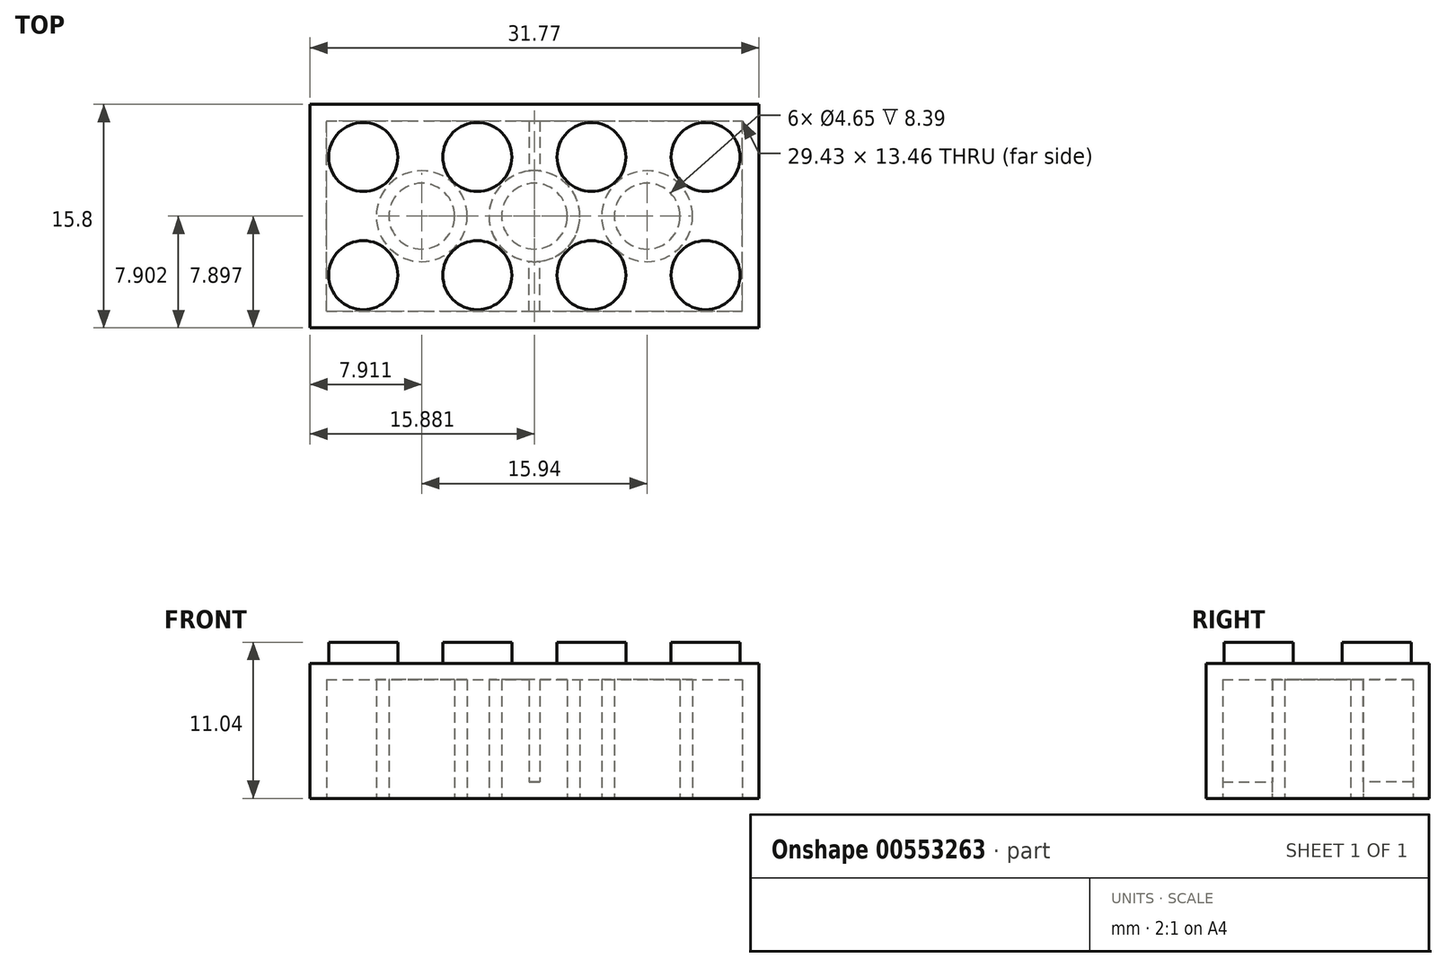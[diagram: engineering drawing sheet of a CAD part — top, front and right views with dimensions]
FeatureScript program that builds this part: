
annotation { "Feature Type Name" : "Feature", "Feature Type Description" : "" }
export const myFeature = defineFeature(function(context is Context, id is Id, definition is map)
    precondition{}
    {
        {
            var Q0;
            Q0=qCreatedBy(makeId("Top.planeOp"),FACE);
            var sketch = newSketch(context, id + "F0", { "sketchPlane" : qUnion([Q0])});
            skLineSegment(sketch, "E0.bottom", {"start": v(-13.15, 22.82) * mm, "end": v(18.62, 22.82) * mm});
            skLineSegment(sketch, "E0.top", {"start": v(-13.15, 7.02) * mm, "end": v(18.62, 7.02) * mm});
            skLineSegment(sketch, "E0.left", {"start": v(-13.15, 22.82) * mm, "end": v(-13.15, 7.02) * mm});
            skLineSegment(sketch, "E0.right", {"start": v(18.62, 22.82) * mm, "end": v(18.62, 7.02) * mm});
            skLineSegment(sketch, "E1.bottom", {"start": v(-11.98, 8.2) * mm, "end": v(17.45, 8.2) * mm});
            skLineSegment(sketch, "E1.top", {"start": v(-11.98, 21.65) * mm, "end": v(17.45, 21.65) * mm});
            skLineSegment(sketch, "E1.left", {"start": v(-11.98, 8.2) * mm, "end": v(-11.98, 21.65) * mm});
            skLineSegment(sketch, "E1.right", {"start": v(17.45, 8.2) * mm, "end": v(17.45, 21.65) * mm});
            skCircle(sketch, "E2", {"center": v(2.73, 14.92) * mm, "radius": 3.21 * mm});
            skCircle(sketch, "E3", {"center": v(10.7, 14.92) * mm, "radius": 3.21 * mm});
            skCircle(sketch, "E4", {"center": v(-5.24, 14.92) * mm, "radius": 3.21 * mm});
            skCircle(sketch, "E5", {"center": v(-5.24, 14.92) * mm, "radius": 2.32 * mm});
            skCircle(sketch, "E6", {"center": v(2.73, 14.92) * mm, "radius": 2.32 * mm});
            skCircle(sketch, "E7", {"center": v(10.7, 14.92) * mm, "radius": 2.32 * mm});
            skLineSegment(sketch, "E8", {"start": v(2.36, 8.2) * mm, "end": v(2.36, 11.72) * mm});
            skLineSegment(sketch, "E9", {"start": v(3.1, 8.2) * mm, "end": v(3.1, 11.72) * mm});
            skLineSegment(sketch, "E10", {"start": v(2.36, 21.65) * mm, "end": v(2.36, 18.11) * mm});
            skLineSegment(sketch, "E11", {"start": v(3.1, 21.65) * mm, "end": v(3.1, 18.11) * mm});
            skSolve(sketch);
        }
        {
            var Q0;
            Q0=qSketchRegion(id+"F0",true);
            var Q1;
            {var subQ3=sQuery(id+"F0.wireOp",EDGE,"E1.left");Q1=makeQuery(id+"F0.imprint","IMPRINT",FACE,{"disambiguationData":[TD([[makeQuery(id+"F0.imprint","IMPRINT",EDGE,{"derivedFrom":subQ3}),-1.0]])]});}
            var Q2;
            {var subQ3=sQuery(id+"F0.wireOp",EDGE,"E1.right");Q2=makeQuery(id+"F0.imprint","IMPRINT",FACE,{"disambiguationData":[TD([[makeQuery(id+"F0.imprint","IMPRINT",EDGE,{"derivedFrom":subQ3}),1.0]])]});}
            var Q3;
            Q3=makeQuery(id+"F0.imprint","IMPRINT",FACE,{"disambiguationData":[TD([[makeQuery(id+"F0.imprint","IMPRINT",EDGE,{"derivedFrom":sQuery(id+"F0.wireOp",EDGE,"E7")}),1.0]])]});
            var Q4;
            Q4=makeQuery(id+"F0.imprint","IMPRINT",FACE,{"disambiguationData":[TD([[makeQuery(id+"F0.imprint","IMPRINT",EDGE,{"derivedFrom":sQuery(id+"F0.wireOp",EDGE,"E5")}),1.0]])]});
            var Q5;
            Q5=makeQuery(id+"F0.imprint","IMPRINT",FACE,{"disambiguationData":[TD([[makeQuery(id+"F0.imprint","IMPRINT",EDGE,{"derivedFrom":sQuery(id+"F0.wireOp",EDGE,"E6")}),1.0]])]});
            var Q6;
            Q6=makeQuery(id+"F0.imprint","IMPRINT",FACE,{"disambiguationData":[TD([[makeQuery(id+"F0.imprint","IMPRINT",EDGE,{"derivedFrom":sQuery(id+"F0.wireOp",EDGE,"E6")}),-1.0]])]});
            var Q7;
            {var subQ0=sQuery(id+"F0.wireOp",EDGE,"E10");Q7=makeQuery(id+"F0.imprint","IMPRINT",FACE,{"disambiguationData":[TD([[makeQuery(id+"F0.imprint","IMPRINT",EDGE,{"derivedFrom":subQ0}),1.0]])]});}
            var Q8;
            Q8=makeQuery(id+"F0.imprint","IMPRINT",FACE,{"disambiguationData":[TD([[makeQuery(id+"F0.imprint","IMPRINT",EDGE,{"derivedFrom":sQuery(id+"F0.wireOp",EDGE,"E3")}),1.0]])]});
            var Q9;
            Q9=makeQuery(id+"F0.imprint","IMPRINT",FACE,{"disambiguationData":[TD([[makeQuery(id+"F0.imprint","IMPRINT",EDGE,{"derivedFrom":sQuery(id+"F0.wireOp",EDGE,"E4")}),1.0]])]});
            var Q10;
            {var subQ0=sQuery(id+"F0.wireOp",EDGE,"E8");Q10=makeQuery(id+"F0.imprint","IMPRINT",FACE,{"disambiguationData":[TD([[makeQuery(id+"F0.imprint","IMPRINT",EDGE,{"derivedFrom":subQ0}),-1.0]])]});}
            extrude(context, id + "F1", {"entities" : qUnion([Q0, Q1, Q2, Q3, Q4, Q5, Q6, Q7, Q8, Q9, Q10]), "depth" : 9.56 * mm});
        }
        {
            var Q0;
            {var subQ3=sQuery(id+"F0.wireOp",EDGE,"E1.left");Q0=makeQuery(id+"F0.imprint","IMPRINT",FACE,{"disambiguationData":[TD([[makeQuery(id+"F0.imprint","IMPRINT",EDGE,{"derivedFrom":subQ3}),-1.0]])]});}
            var Q1;
            {var subQ3=sQuery(id+"F0.wireOp",EDGE,"E1.right");Q1=makeQuery(id+"F0.imprint","IMPRINT",FACE,{"disambiguationData":[TD([[makeQuery(id+"F0.imprint","IMPRINT",EDGE,{"derivedFrom":subQ3}),1.0]])]});}
            var Q2;
            Q2=makeQuery(id+"F0.imprint","IMPRINT",FACE,{"disambiguationData":[TD([[makeQuery(id+"F0.imprint","IMPRINT",EDGE,{"derivedFrom":sQuery(id+"F0.wireOp",EDGE,"E7")}),1.0]])]});
            var Q3;
            Q3=makeQuery(id+"F0.imprint","IMPRINT",FACE,{"disambiguationData":[TD([[makeQuery(id+"F0.imprint","IMPRINT",EDGE,{"derivedFrom":sQuery(id+"F0.wireOp",EDGE,"E6")}),1.0]])]});
            var Q4;
            Q4=makeQuery(id+"F0.imprint","IMPRINT",FACE,{"disambiguationData":[TD([[makeQuery(id+"F0.imprint","IMPRINT",EDGE,{"derivedFrom":sQuery(id+"F0.wireOp",EDGE,"E5")}),1.0]])]});
            extrude(context, id + "F2", {"entities" : qUnion([Q0, Q1, Q2, Q3, Q4]), "operationType" : NewBodyOperationType.REMOVE, "depth" : 8.4 * mm});
        }
        {
            var Q0;
            {var subQ0=sQuery(id+"F0.wireOp",EDGE,"E8");Q0=makeQuery(id+"F0.imprint","IMPRINT",FACE,{"disambiguationData":[TD([[makeQuery(id+"F0.imprint","IMPRINT",EDGE,{"derivedFrom":subQ0}),-1.0]])]});}
            var Q1;
            {var subQ0=sQuery(id+"F0.wireOp",EDGE,"E10");Q1=makeQuery(id+"F0.imprint","IMPRINT",FACE,{"disambiguationData":[TD([[makeQuery(id+"F0.imprint","IMPRINT",EDGE,{"derivedFrom":subQ0}),1.0]])]});}
            extrude(context, id + "F3", {"entities" : qUnion([Q0, Q1]), "operationType" : NewBodyOperationType.REMOVE, "depth" : 1.17 * mm});
        }
        {
            var Q0;
            Q0=makeQuery(id+"F1.opExtrude","CAP_FACE",FACE,{"disambiguationData":[OSD([sQuery(id+"F0.wireOp",EDGE,"E0.bottom"),sQuery(id+"F0.wireOp",EDGE,"E0.top"),sQuery(id+"F0.wireOp",EDGE,"E0.left"),sQuery(id+"F0.wireOp",EDGE,"E0.right")])],"isStart":false});
            var sketch = newSketch(context, id + "F4", { "sketchPlane" : qUnion([Q0])});
            skCircle(sketch, "E12", {"center": v(-9.37, 19.1) * mm, "radius": 2.44 * mm});
            skCircle(sketch, "E13", {"center": v(-1.3, 19.1) * mm, "radius": 2.44 * mm});
            skCircle(sketch, "E14", {"center": v(6.77, 19.1) * mm, "radius": 2.44 * mm});
            skCircle(sketch, "E15", {"center": v(14.84, 19.1) * mm, "radius": 2.44 * mm});
            skCircle(sketch, "E16", {"center": v(-9.37, 10.74) * mm, "radius": 2.44 * mm});
            skCircle(sketch, "E17", {"center": v(-1.3, 10.74) * mm, "radius": 2.44 * mm});
            skCircle(sketch, "E18", {"center": v(6.77, 10.74) * mm, "radius": 2.44 * mm});
            skCircle(sketch, "E19", {"center": v(14.84, 10.74) * mm, "radius": 2.44 * mm});
            skSolve(sketch);
        }
        {
            var Q0;
            Q0=makeQuery(id+"F4.imprint","IMPRINT",FACE,{"disambiguationData":[TD([[makeQuery(id+"F4.imprint","IMPRINT",EDGE,{"derivedFrom":sQuery(id+"F4.wireOp",EDGE,"E12")}),1.0]])]});
            var Q1;
            Q1=makeQuery(id+"F4.imprint","IMPRINT",FACE,{"disambiguationData":[TD([[makeQuery(id+"F4.imprint","IMPRINT",EDGE,{"derivedFrom":sQuery(id+"F4.wireOp",EDGE,"E16")}),1.0]])]});
            var Q2;
            Q2=makeQuery(id+"F4.imprint","IMPRINT",FACE,{"disambiguationData":[TD([[makeQuery(id+"F4.imprint","IMPRINT",EDGE,{"derivedFrom":sQuery(id+"F4.wireOp",EDGE,"E13")}),1.0]])]});
            var Q3;
            Q3=makeQuery(id+"F4.imprint","IMPRINT",FACE,{"disambiguationData":[TD([[makeQuery(id+"F4.imprint","IMPRINT",EDGE,{"derivedFrom":sQuery(id+"F4.wireOp",EDGE,"E17")}),1.0]])]});
            var Q4;
            Q4=makeQuery(id+"F4.imprint","IMPRINT",FACE,{"disambiguationData":[TD([[makeQuery(id+"F4.imprint","IMPRINT",EDGE,{"derivedFrom":sQuery(id+"F4.wireOp",EDGE,"E14")}),1.0]])]});
            var Q5;
            Q5=makeQuery(id+"F4.imprint","IMPRINT",FACE,{"disambiguationData":[TD([[makeQuery(id+"F4.imprint","IMPRINT",EDGE,{"derivedFrom":sQuery(id+"F4.wireOp",EDGE,"E18")}),1.0]])]});
            var Q6;
            Q6=makeQuery(id+"F4.imprint","IMPRINT",FACE,{"disambiguationData":[TD([[makeQuery(id+"F4.imprint","IMPRINT",EDGE,{"derivedFrom":sQuery(id+"F4.wireOp",EDGE,"E15")}),1.0]])]});
            var Q7;
            Q7=makeQuery(id+"F4.imprint","IMPRINT",FACE,{"disambiguationData":[TD([[makeQuery(id+"F4.imprint","IMPRINT",EDGE,{"derivedFrom":sQuery(id+"F4.wireOp",EDGE,"E19")}),1.0]])]});
            extrude(context, id + "F5", {"entities" : qUnion([Q0, Q1, Q2, Q3, Q4, Q5, Q6, Q7]), "operationType" : NewBodyOperationType.ADD, "depth" : 1.48 * mm});
        }
        {
            var Q0;
            Q0=makeQuery(id+"F1.opExtrude","SWEPT_BODY",BODY,{"disambiguationData":[OSD([sQuery(id+"F0.wireOp",EDGE,"E0.bottom"),sQuery(id+"F0.wireOp",EDGE,"E0.top"),sQuery(id+"F0.wireOp",EDGE,"E0.left"),sQuery(id+"F0.wireOp",EDGE,"E0.right")])]});
            transform(context, id + "F6", {"entities" : qUnion([Q0]), "transformType" : TransformType.TRANSLATION_3D, "dx" : 0 * mm, "dy" : 0 * mm, "dz" : 0 * mm, "makeCopy" : true});
        }
    });
